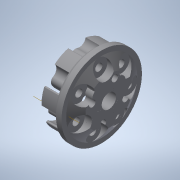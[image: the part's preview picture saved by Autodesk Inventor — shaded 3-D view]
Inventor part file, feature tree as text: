
AUTODESK INVENTOR PART (.ipt)
format: ipt  version: 2020 (Build 240168000, 168)  size: 721,408 bytes
history: native  units: in
note: dims shown in document units (in); Inventor stores cm internally (conversion verified against a paired STEP export)
features: other x4, sketch x4, extrude x2, plane x2, mirror x1
ambient origin geometry x8: Origin, YZ Plane, XZ Plane, XY Plane, X Axis, Y Axis, Z Axis, Center Point
bodies: Solid1 (feature_tree)
feature tree (13):
  other  "Mecanum Adaptor 1.3.ipt"
  extrude  "Extrusion1"  Depth=0.217in TaperAngle=0.0deg
  extrude  "Extrusion2"  Depth=0.1406in
  mirror  "Mirror1"
  other  "Solid1::Mecanum Adaptor 1.3.ipt"
  other  "TaggingFeature1"
  sketch  "Sketch6"  dims[d0=0.3937in]
  sketch  "Sketch11"  dims[d4=0.4724in d5=0.0in d6=0.0787in d7=1.757in d8=1.6061in d9=0.0in d10=90.0deg d11=0.0in d12=90.0deg d13=0.1181in d14=0.0in d15=0.1575in d16=2.7559in d21=0.0in d23=0.0in d25=0.0in d26=0.1575in d27=0.0in d28=0.374in d29=2.7559in d33=0.0787in d34=0.0in d35=0.1378in d36=0.0in d38=0.0in d55=2.7559in d60=0.0in d61=0.2756in d62=0.7874in d64=0.446in d65=0.7874in d67=0.446in d70=0.0984in d71=0.0in d72=0.2638in d73=0.1575in d75=0.2638in d76=0.1575in d78=0.2638in d79=0.1575in d81=0.2638in d82=0.1575in d84=0.2638in d85=0.1575in d87=0.2638in d88=0.1575in d90=0.2638in d91=0.1575in d93=0.1575in d2=360.0deg d18=360.0deg d31=360.0deg d57=360.0deg d1=0.217in d3=0.0in]
  plane  "Work Plane1"
  plane  "Work Plane2"
  other  "Work Axis1"
  sketch  "Sketch18"  dims[d19=0.1406in d20=0.1406in]
  sketch  "Sketch19"  dims[d22=0.1406in d24=0.1406in d30=0.7795in d32=0.0in]
